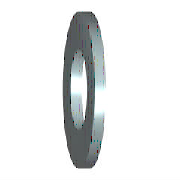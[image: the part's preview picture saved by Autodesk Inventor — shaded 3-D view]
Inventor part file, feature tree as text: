
AUTODESK INVENTOR PART (.ipt)
format: ipt  version: 2024.3 (Build 283343000, 343)  size: 104,960 bytes
history: native  units: mm (DEFAULTED — no unit token found)
features: other x1, plane x1
ambient origin geometry x7: Origin, YZ Plane, XY Plane, X Axis, Y Axis, Z Axis, Center Point
bodies: Solid1 (feature_tree), Body (feature_tree)
feature tree (2):
  other  "Work Axis1"
  plane  "Work Plane1"
